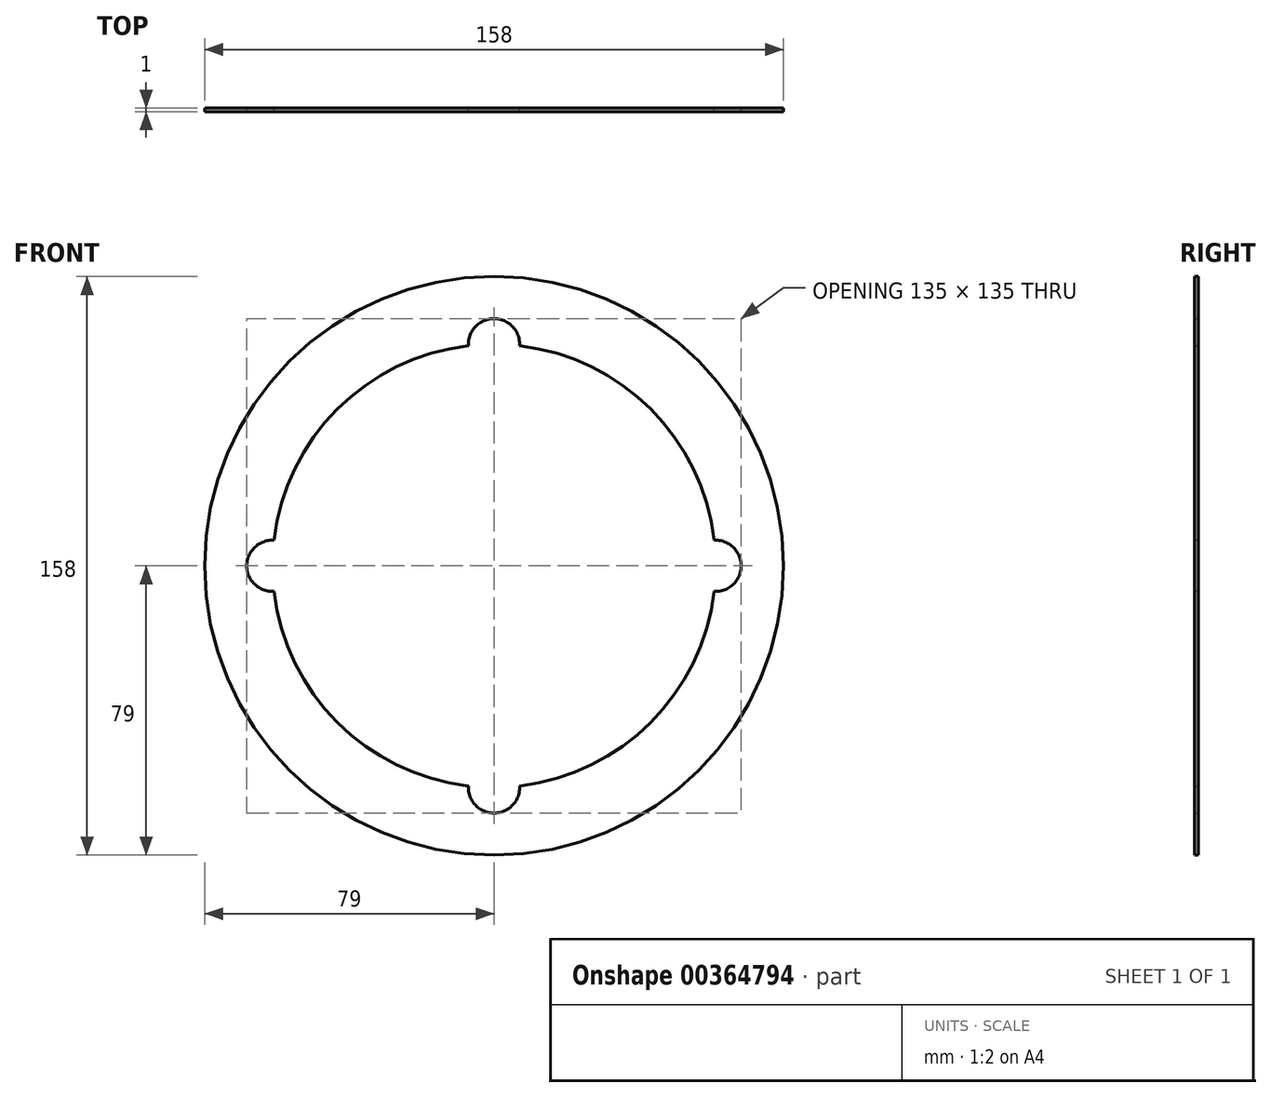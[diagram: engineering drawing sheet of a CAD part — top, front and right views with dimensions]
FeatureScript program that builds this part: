
annotation { "Feature Type Name" : "Feature", "Feature Type Description" : "" }
export const myFeature = defineFeature(function(context is Context, id is Id, definition is map)
    precondition{}
    {
        {
            var Q0;
            Q0=qCreatedBy(makeId("Front.planeOp"),FACE);
            var sketch = newSketch(context, id + "F0", { "sketchPlane" : qUnion([Q0])});
            skCircle(sketch, "E0", {"center": v(0, 0) * mm, "radius": 79 * mm});
            skCircle(sketch, "E1", {"center": v(0, 0) * mm, "radius": 60.5 * mm});
            skCircle(sketch, "E2", {"center": v(0, 0) * mm, "radius": 39.5 * mm});
            skLineSegment(sketch, "E3", {"start": v(0, 0) * mm, "end": v(0, 60.5) * mm});
            skCircle(sketch, "E4", {"center": v(0, 60.5) * mm, "radius": 7 * mm});
            skCircle(sketch, "E5.1.0", {"center": v(-60.5, 0) * mm, "radius": 7 * mm});
            skCircle(sketch, "E5.2.0", {"center": v(0, -60.5) * mm, "radius": 7 * mm});
            skCircle(sketch, "E5.3.0", {"center": v(60.5, 0) * mm, "radius": 7 * mm});
            skSolve(sketch);
        }
        {
            var Q0;
            Q0=makeQuery(id+"F0.imprint","IMPRINT",FACE,{"disambiguationData":[TD([[makeQuery(id+"F0.imprint","IMPRINT",EDGE,{"derivedFrom":sQuery(id+"F0.wireOp",EDGE,"E0")}),1.0]])]});
            var Q1;
            {var subQ8=sQuery(id+"F0.wireOp",EDGE,"E2");var subQ9=makeQuery(id+"F0.imprint","IMPRINT",VERTEX,{"disambiguationData":[OD(0.0)],"derivedFrom":subQ8});Q1=makeQuery(id+"F0.imprint","IMPRINT",FACE,{"disambiguationData":[TD([[makeQuery(id+"F0.imprint","IMPRINT",EDGE,{"disambiguationData":[TD([[subQ9,1.0]])],"derivedFrom":subQ8}),-1.0]])]});}
            extrude(context, id + "F1", {"entities" : qUnion([Q0, Q1]), "depth" : 1 * mm, "offsetDistance" : 25 * mm});
        }
    });
